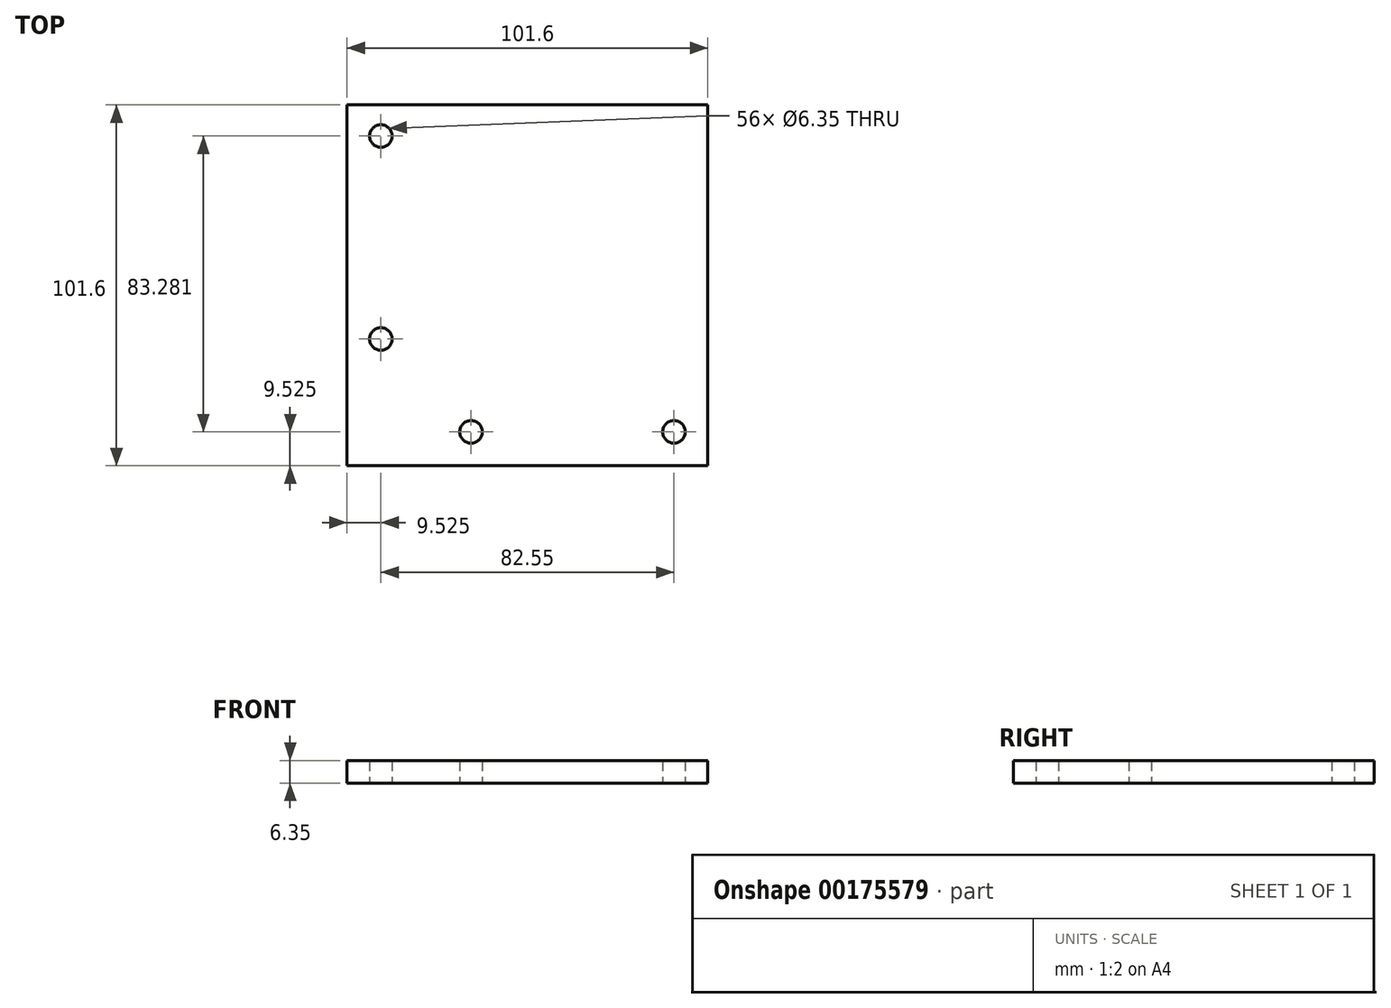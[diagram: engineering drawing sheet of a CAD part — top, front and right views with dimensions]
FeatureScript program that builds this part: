
annotation { "Feature Type Name" : "Feature", "Feature Type Description" : "" }
export const myFeature = defineFeature(function(context is Context, id is Id, definition is map)
    precondition{}
    {
        {
            var Q0;
            Q0=qCreatedBy(makeId("Top.planeOp"),FACE);
            var sketch = newSketch(context, id + "F0", { "sketchPlane" : qUnion([Q0])});
            skLineSegment(sketch, "E0.bottom", {"start": v(-50.8, 50.8) * mm, "end": v(50.8, 50.8) * mm});
            skLineSegment(sketch, "E0.top", {"start": v(-50.8, -50.8) * mm, "end": v(50.8, -50.8) * mm});
            skLineSegment(sketch, "E0.left", {"start": v(-50.8, 50.8) * mm, "end": v(-50.8, -50.8) * mm});
            skLineSegment(sketch, "E0.right", {"start": v(50.8, 50.8) * mm, "end": v(50.8, -50.8) * mm});
            skPoint(sketch, "E0.middle", {"position": v(0, 0) * mm});
            skLineSegment(sketch, "E1.bottom", {"start": v(50.8, 50.8) * mm, "end": v(-31.75, 50.8) * mm});
            skLineSegment(sketch, "E1.top", {"start": v(50.8, -31.75) * mm, "end": v(-31.75, -31.75) * mm});
            skLineSegment(sketch, "E1.left", {"start": v(50.8, 50.8) * mm, "end": v(50.8, -31.75) * mm});
            skLineSegment(sketch, "E1.right", {"start": v(-31.75, 50.8) * mm, "end": v(-31.75, -31.75) * mm});
            skPoint(sketch, "E2", {"position": v(-41.27, 50.8) * mm});
            skPoint(sketch, "E3", {"position": v(50.8, -41.28) * mm});
            skCircle(sketch, "E4", {"center": v(41.27, -41.28) * mm, "radius": 3.17 * mm});
            skCircle(sketch, "E5", {"center": v(-15.88, -41.28) * mm, "radius": 3.18 * mm});
            skCircle(sketch, "E6.MirrorC", {"center": v(-41.27, 42) * mm, "radius": 3.17 * mm});
            skCircle(sketch, "E7", {"center": v(-41.27, -15.14) * mm, "radius": 3.18 * mm});
            skSolve(sketch);
        }
        {
            var Q0;
            {var subQ5=sQuery(id+"F0.wireOp",EDGE,"E0.left");Q0=makeQuery(id+"F0.imprint","IMPRINT",FACE,{"disambiguationData":[TD([[makeQuery(id+"F0.imprint","IMPRINT",EDGE,{"derivedFrom":subQ5}),1.0]])]});}
            var Q1;
            {var subQ7=sQuery(id+"F0.wireOp",EDGE,"E0.right");Q1=makeQuery(id+"F0.imprint","IMPRINT",FACE,{"disambiguationData":[TD([[makeQuery(id+"F0.imprint","IMPRINT",EDGE,{"derivedFrom":subQ7}),-1.0]])]});}
            extrude(context, id + "F1", {"entities" : qUnion([Q0, Q1]), "depth" : 6.35 * mm});
        }
    });
